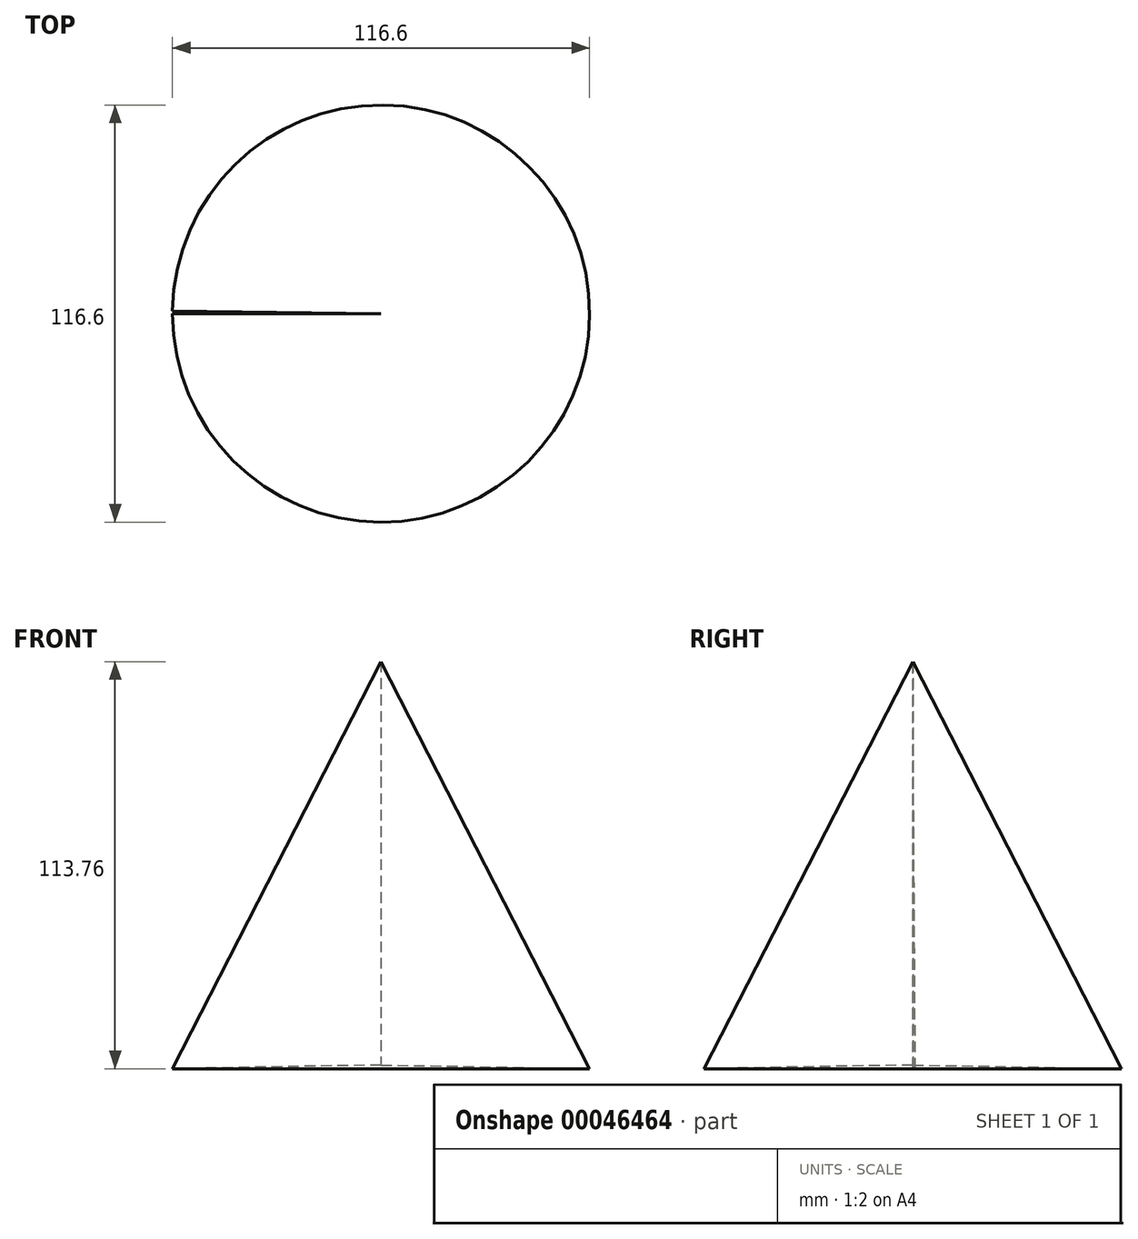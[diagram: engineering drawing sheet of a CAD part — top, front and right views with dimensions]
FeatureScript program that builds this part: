
annotation { "Feature Type Name" : "Feature", "Feature Type Description" : "" }
export const myFeature = defineFeature(function(context is Context, id is Id, definition is map)
    precondition{}
    {
        {
            var Q0;
            Q0=qCreatedBy(makeId("Front.planeOp"),FACE);
            var sketch = newSketch(context, id + "F0", { "sketchPlane" : qUnion([Q0])});
            skLineSegment(sketch, "E0", {"start": v(0, 65.15) * mm, "end": v(0, -47.59) * mm});
            skLineSegment(sketch, "E1", {"start": v(-58.3, -48.61) * mm, "end": v(0, 65.15) * mm});
            skLineSegment(sketch, "E2", {"start": v(0, -47.59) * mm, "end": v(-58.3, -48.61) * mm});
            skSolve(sketch);
        }
        {
            var Q0;
            Q0=makeQuery(id+"F0.imprint","IMPRINT",FACE,{"disambiguationData":[TD([[makeQuery(id+"F0.imprint","IMPRINT",EDGE,{"derivedFrom":sQuery(id+"F0.wireOp",EDGE,"E0")}),-1.0]])]});
            var Q1;
            Q1=sQuery(id+"F0.wireOp",EDGE,"E0");
            revolve(context, id + "F1", {"entities" : qUnion([Q0]), "axis" : qUnion([Q1]), "revolveType" : RevolveType.ONE_DIRECTION, "oppositeDirection" : true, "angle" : 359.3 * degree});
        }
    });
